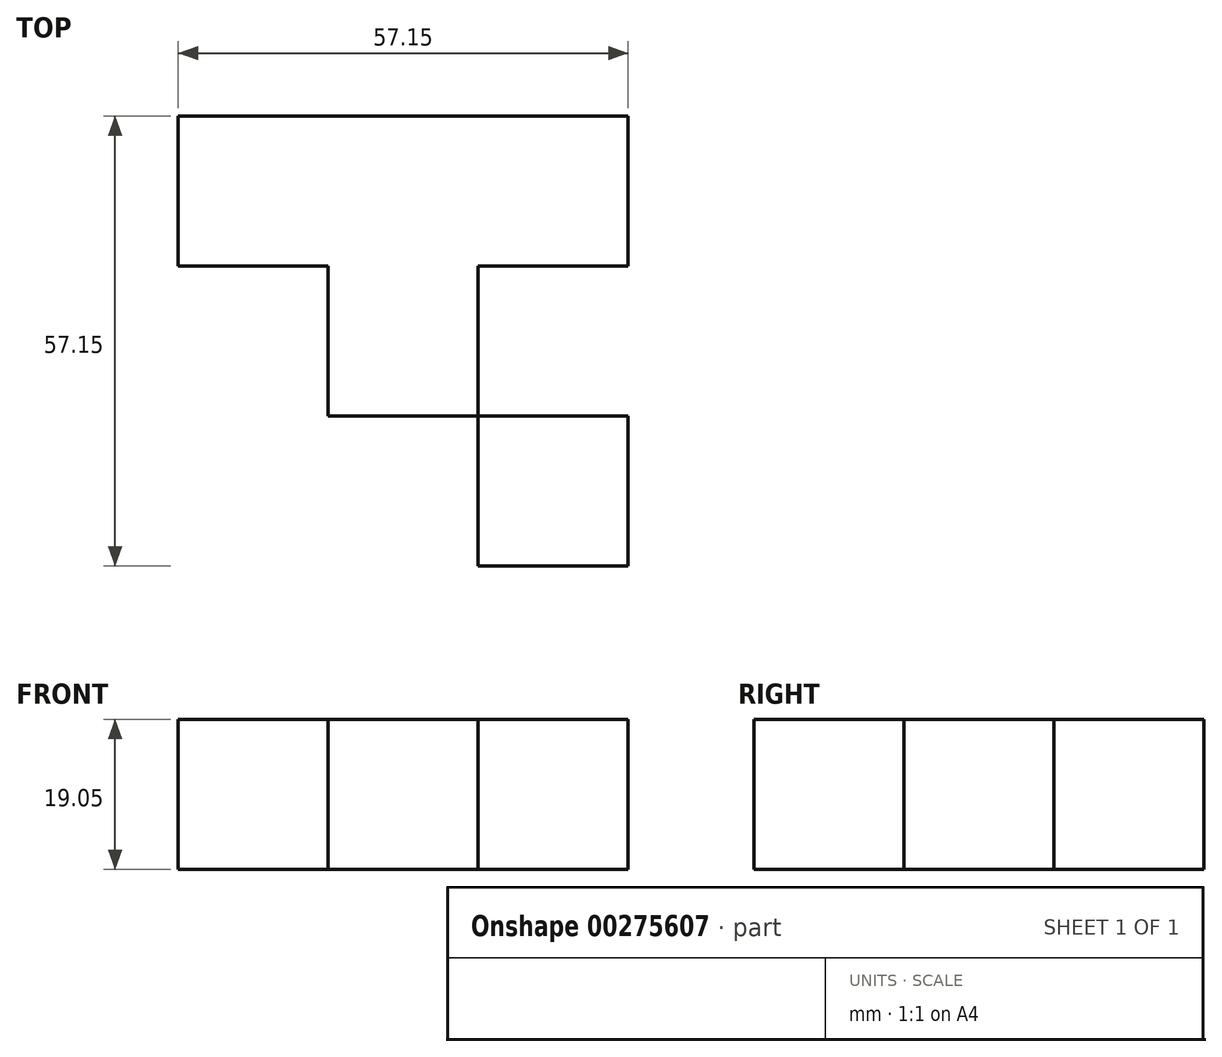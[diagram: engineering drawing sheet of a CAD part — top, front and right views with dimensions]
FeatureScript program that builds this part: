
annotation { "Feature Type Name" : "Feature", "Feature Type Description" : "" }
export const myFeature = defineFeature(function(context is Context, id is Id, definition is map)
    precondition{}
    {
        {
            var Q0;
            Q0=qCreatedBy(makeId("Top.planeOp"),FACE);
            var sketch = newSketch(context, id + "F0", { "sketchPlane" : qUnion([Q0])});
            skLineSegment(sketch, "E0.bottom", {"start": v(-53.39, 53.46) * mm, "end": v(-34.34, 53.46) * mm});
            skLineSegment(sketch, "E0.top", {"start": v(-53.39, 34.41) * mm, "end": v(-34.34, 34.41) * mm});
            skLineSegment(sketch, "E0.left", {"start": v(-53.39, 53.46) * mm, "end": v(-53.39, 34.41) * mm});
            skLineSegment(sketch, "E0.right", {"start": v(-34.34, 53.46) * mm, "end": v(-34.34, 34.41) * mm});
            skLineSegment(sketch, "E1.bottom", {"start": v(-34.34, 53.46) * mm, "end": v(-15.29, 53.46) * mm});
            skLineSegment(sketch, "E1.top", {"start": v(-34.34, 34.41) * mm, "end": v(-15.29, 34.41) * mm});
            skLineSegment(sketch, "E1.right", {"start": v(-15.29, 53.46) * mm, "end": v(-15.29, 34.41) * mm});
            skLineSegment(sketch, "E2.bottom", {"start": v(-15.29, 53.46) * mm, "end": v(3.76, 53.46) * mm});
            skLineSegment(sketch, "E2.top", {"start": v(-15.29, 34.41) * mm, "end": v(3.76, 34.41) * mm});
            skLineSegment(sketch, "E2.right", {"start": v(3.76, 53.46) * mm, "end": v(3.76, 34.41) * mm});
            skLineSegment(sketch, "E3.bottom", {"start": v(3.76, 34.41) * mm, "end": v(-15.29, 34.41) * mm});
            skLineSegment(sketch, "E3.top", {"start": v(3.76, 15.36) * mm, "end": v(-15.29, 15.36) * mm});
            skLineSegment(sketch, "E3.left", {"start": v(3.76, 34.41) * mm, "end": v(3.76, 15.36) * mm});
            skLineSegment(sketch, "E3.right", {"start": v(-15.29, 34.41) * mm, "end": v(-15.29, 15.36) * mm});
            skLineSegment(sketch, "E4.top", {"start": v(3.76, -3.69) * mm, "end": v(-15.29, -3.69) * mm});
            skLineSegment(sketch, "E4.left", {"start": v(3.76, 15.36) * mm, "end": v(3.76, -3.69) * mm});
            skLineSegment(sketch, "E4.right", {"start": v(-15.29, 15.36) * mm, "end": v(-15.29, -3.69) * mm});
            skLineSegment(sketch, "E5.top", {"start": v(-34.34, 15.36) * mm, "end": v(-15.29, 15.36) * mm});
            skLineSegment(sketch, "E5.left", {"start": v(-34.34, 34.41) * mm, "end": v(-34.34, 15.36) * mm});
            skSolve(sketch);
        }
        {
            var Q0;
            Q0=makeQuery(id+"F0.imprint","IMPRINT",FACE,{"disambiguationData":[TD([[makeQuery(id+"F0.imprint","IMPRINT",EDGE,{"derivedFrom":sQuery(id+"F0.wireOp",EDGE,"E0.bottom")}),-1.0]])]});
            var Q1;
            Q1=makeQuery(id+"F0.imprint","IMPRINT",FACE,{"disambiguationData":[TD([[makeQuery(id+"F0.imprint","IMPRINT",EDGE,{"derivedFrom":sQuery(id+"F0.wireOp",EDGE,"E1.bottom")}),-1.0]])]});
            var Q2;
            Q2=makeQuery(id+"F0.imprint","IMPRINT",FACE,{"disambiguationData":[TD([[makeQuery(id+"F0.imprint","IMPRINT",EDGE,{"derivedFrom":sQuery(id+"F0.wireOp",EDGE,"E2.bottom")}),-1.0]])]});
            var Q3;
            Q3=makeQuery(id+"F0.imprint","IMPRINT",FACE,{"disambiguationData":[TD([[makeQuery(id+"F0.imprint","IMPRINT",EDGE,{"derivedFrom":sQuery(id+"F0.wireOp",EDGE,"E3.bottom")}),1.0]])]});
            var Q4;
            Q4=makeQuery(id+"F0.imprint","IMPRINT",FACE,{"disambiguationData":[TD([[makeQuery(id+"F0.imprint","IMPRINT",EDGE,{"derivedFrom":sQuery(id+"F0.wireOp",EDGE,"E1.top")}),-1.0]])]});
            var Q5;
            Q5=makeQuery(id+"F0.imprint","IMPRINT",FACE,{"disambiguationData":[TD([[makeQuery(id+"F0.imprint","IMPRINT",EDGE,{"derivedFrom":sQuery(id+"F0.wireOp",EDGE,"E3.top")}),1.0]])]});
            extrude(context, id + "F1", {"entities" : qUnion([Q0, Q1, Q2, Q3, Q4, Q5]), "depth" : 19.05 * mm});
        }
    });
